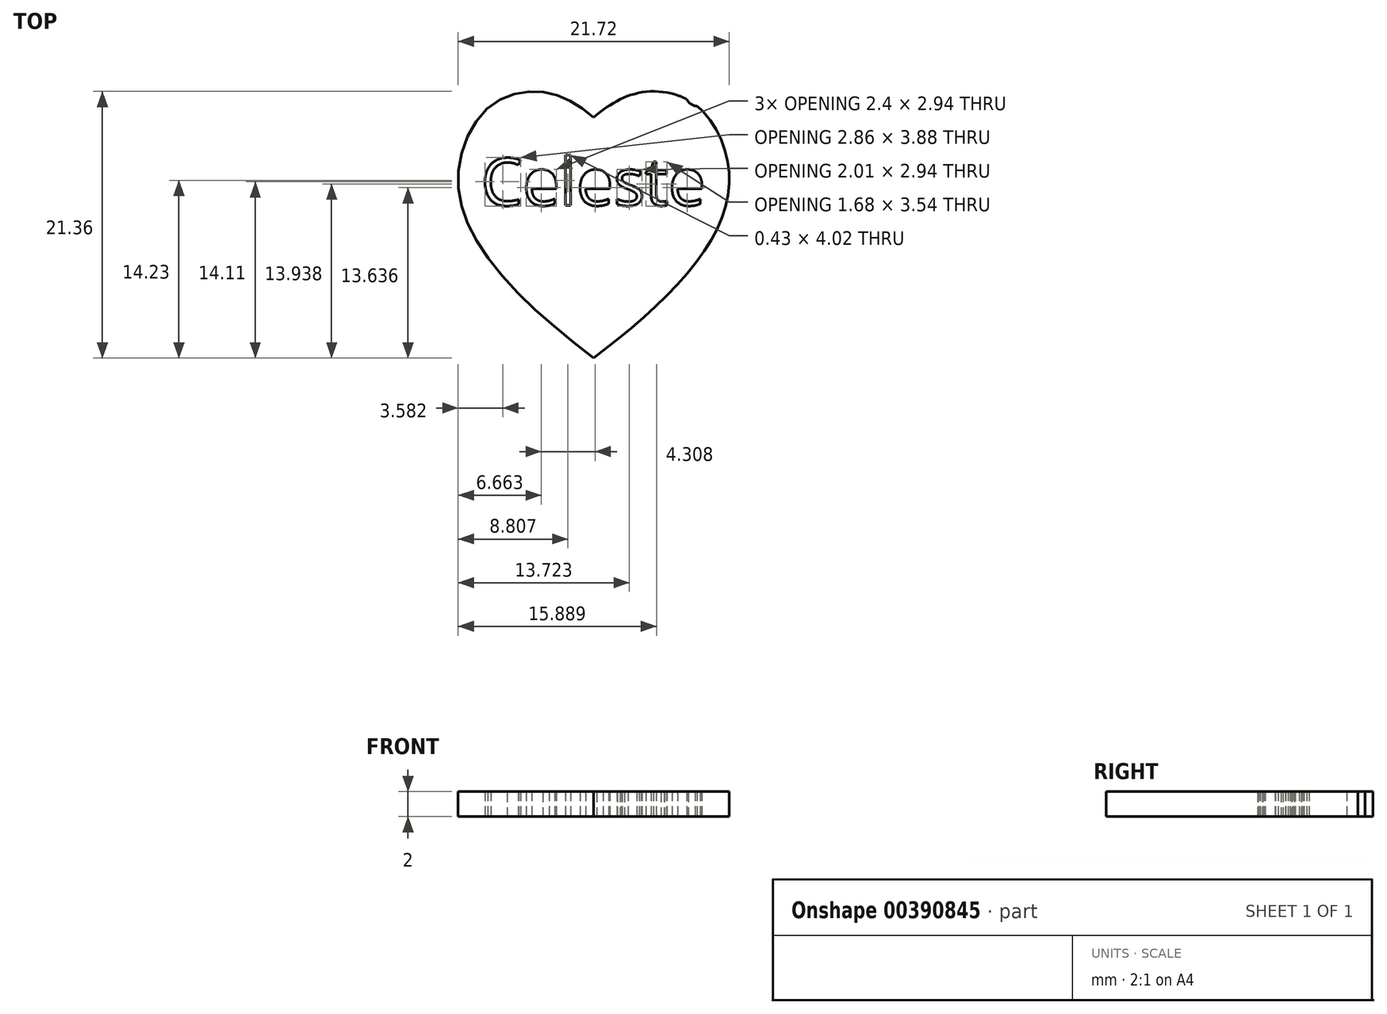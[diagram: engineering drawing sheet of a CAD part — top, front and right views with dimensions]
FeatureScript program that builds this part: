
annotation { "Feature Type Name" : "Feature", "Feature Type Description" : "" }
export const myFeature = defineFeature(function(context is Context, id is Id, definition is map)
    precondition{}
    {
        {
            var Q0;
            Q0=qCreatedBy(makeId("Top.planeOp"),FACE);
            var sketch = newSketch(context, id + "F0", { "sketchPlane" : qUnion([Q0])});
            skFitSpline(sketch, "E0", {"points": [v(0, -5.15) * mm, v(-8.76, 3.25) * mm, v(-10.82, 9.97) * mm, v(-8.05, 15.2) * mm, v(-3.65, 16.1) * mm, v(0, 14.13) * mm], "startDerivative": vector(-36.7, 27.7) * mm, "endDerivative": vector(21.68, -18.07) * mm});
            skFitSpline(sketch, "E1.MirrorCS", {"points": [v(0, -5.15) * mm, v(8.76, 3.25) * mm, v(10.82, 9.97) * mm, v(8.05, 15.2) * mm, v(3.65, 16.1) * mm, v(0, 14.13) * mm], "startDerivative": vector(36.7, 27.7) * mm, "endDerivative": vector(-21.68, -18.07) * mm});
            skArc(sketch, "E2", {"start": v(8.77, 14.57) * mm, "mid": v(9.17, 17.25) * mm, "end": v(6.85, 15.85) * mm});
            skCircle(sketch, "E3", {"center": v(8.34, 16) * mm, "radius": 0.98 * mm});
            skText(sketch, "E4", { "text": "Celeste", "fontName": "OpenSans-Regular.ttf"});
            const initialGuessF0  = {"E4": [-0.00903, 0.00707, 1, 0, 0.00381]};
            skSetInitialGuess(sketch, initialGuessF0);
            skSolve(sketch);
        }
        {
            var Q0;
            Q0=makeQuery(id+"F0.imprint","IMPRINT",FACE,{"disambiguationData":[TD([[makeQuery(id+"F0.imprint","IMPRINT",EDGE,{"derivedFrom":sQuery(id+"F0.wireOp",EDGE,"E0")}),-1.0]])]});
            extrude(context, id + "F1", {"entities" : qUnion([Q0]), "depth" : 2 * mm});
        }
    });
